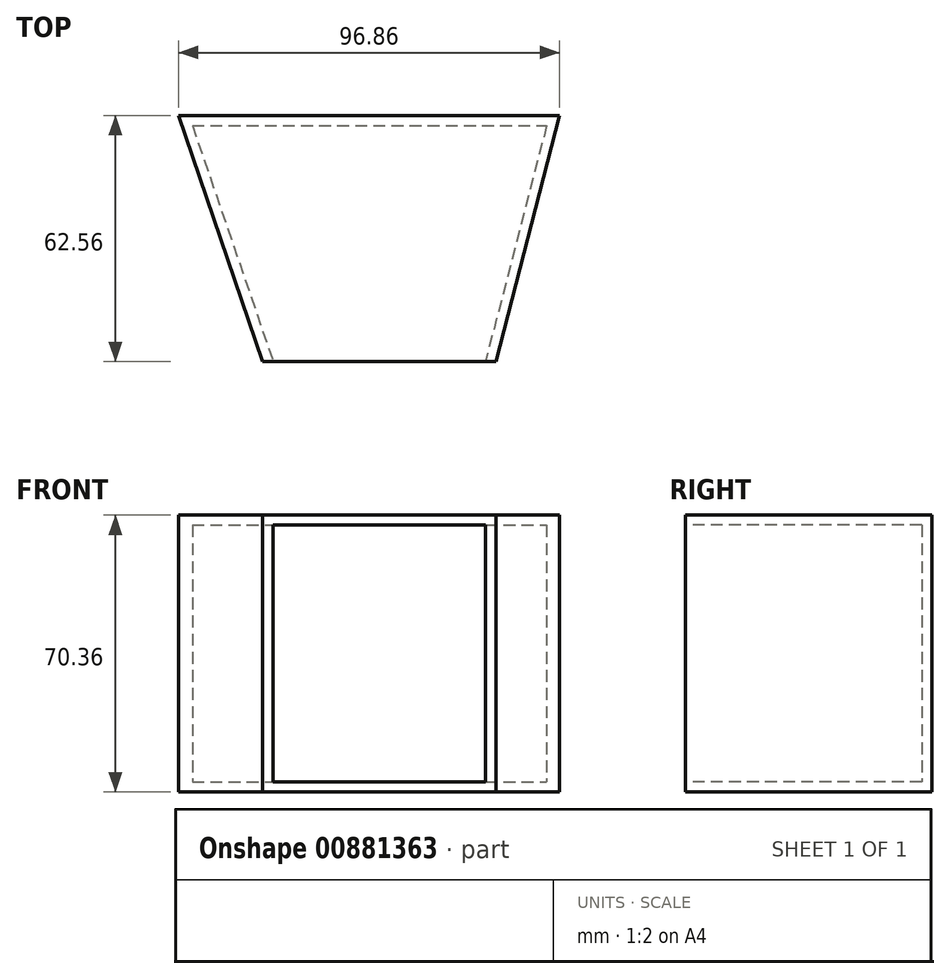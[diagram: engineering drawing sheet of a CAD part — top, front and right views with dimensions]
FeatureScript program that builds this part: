
annotation { "Feature Type Name" : "Feature", "Feature Type Description" : "" }
export const myFeature = defineFeature(function(context is Context, id is Id, definition is map)
    precondition{}
    {
        {
            var Q0;
            Q0=qCreatedBy(makeId("Top.planeOp"),FACE);
            var sketch = newSketch(context, id + "F0", { "sketchPlane" : qUnion([Q0])});
            skLineSegment(sketch, "E0.bottom", {"start": v(-48.75, 37.45) * mm, "end": v(48.11, 37.45) * mm});
            skLineSegment(sketch, "E0.top", {"start": v(-27.32, -25.11) * mm, "end": v(31.9, -25.11) * mm});
            skLineSegment(sketch, "E0.left", {"start": v(-48.75, 37.45) * mm, "end": v(-27.32, -25.11) * mm});
            skLineSegment(sketch, "E0.right", {"start": v(48.11, 37.45) * mm, "end": v(31.9, -25.11) * mm});
            skSolve(sketch);
        }
        {
            var Q0;
            Q0 = qSketchRegion(id + "F0", true);
            extrude(context, id + "F1", {"entities" : qUnion([Q0]), "depth" : 70.36 * mm, "offsetDistance" : 25.4 * mm});
        }
        {
            var Q0;
            Q0=makeQuery(id+"F1.opExtrude","SWEPT_FACE",FACE,{"disambiguationData":[OSD([sQuery(id+"F0.wireOp",EDGE,"E0.right")])]});
            var sketch = newSketch(context, id + "F2", { "sketchPlane" : qUnion([Q0])});
            skSolve(sketch);
        }
        {
            var Q0;
            Q0=makeQuery(id+"F1.opExtrude","SWEPT_FACE",FACE,{"disambiguationData":[OSD([sQuery(id+"F0.wireOp",EDGE,"E0.top")])]});
            shell(context, id + "F3", {"entities" : qUnion([Q0]), "thickness" : 2.54 * mm});
        }
    });
